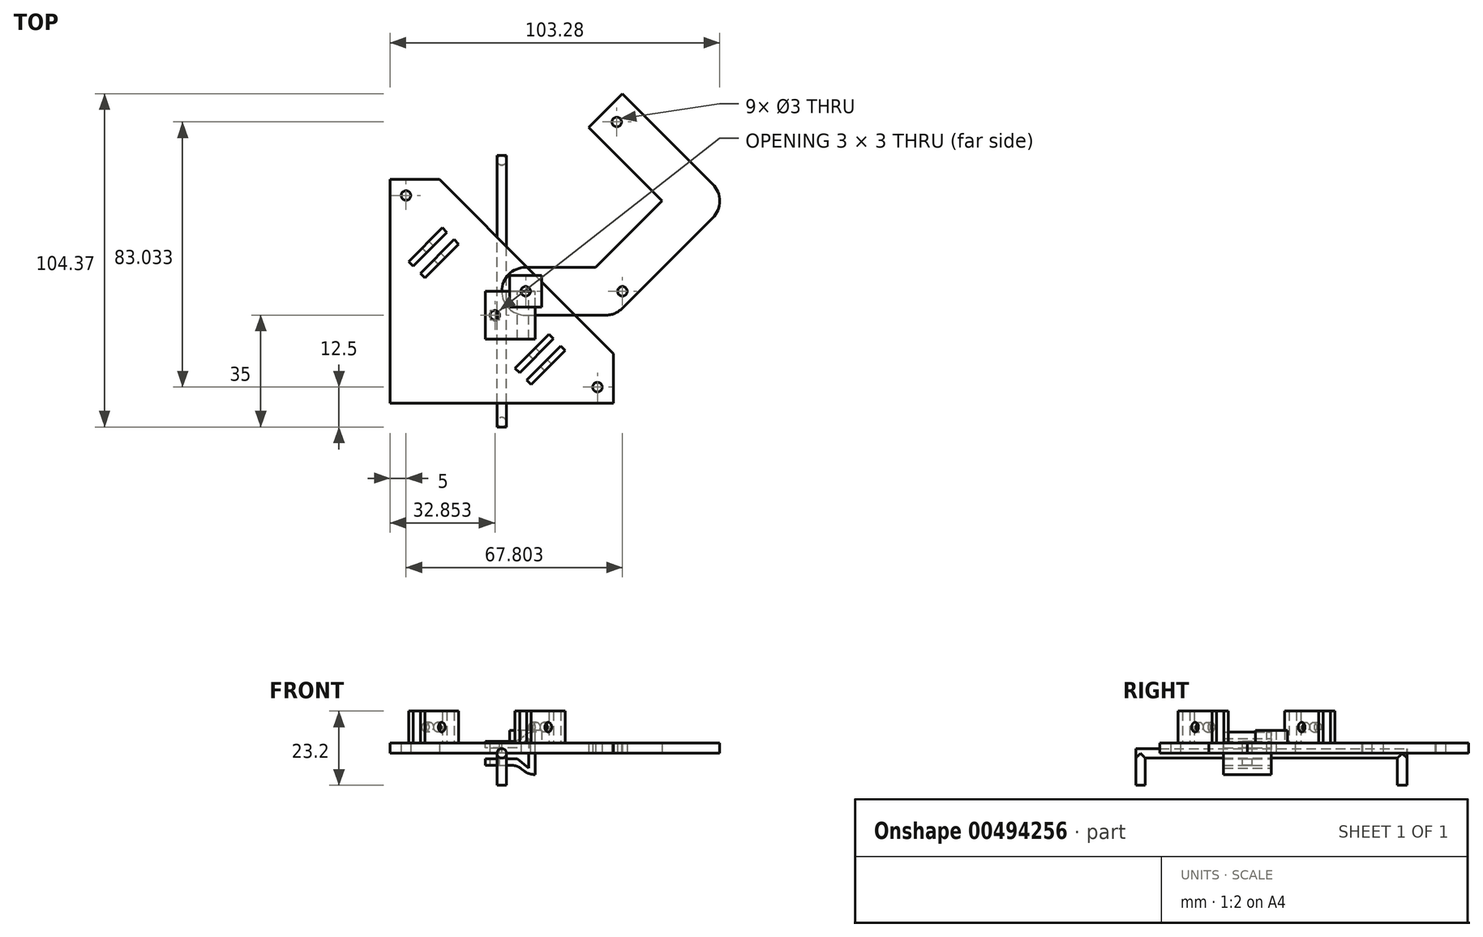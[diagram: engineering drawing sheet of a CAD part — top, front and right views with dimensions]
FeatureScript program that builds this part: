
annotation { "Feature Type Name" : "Feature", "Feature Type Description" : "" }
export const myFeature = defineFeature(function(context is Context, id is Id, definition is map)
    precondition{}
    {
        {
            var Q0;
            Q0=qCreatedBy(makeId("Top.planeOp"),FACE);
            var sketch = newSketch(context, id + "F0", { "sketchPlane" : qUnion([Q0])});
            skArc(sketch, "E0", {"start": v(7.5, 7.5) * mm, "mid": v(0, 0) * mm, "end": v(7.5, -7.5) * mm});
            skPoint(sketch, "E1", {"position": v(0, 0) * mm});
            skArc(sketch, "E2", {"start": v(32.5, -7.5) * mm, "mid": v(39.43, 2.87) * mm, "end": v(27.2, 5.3) * mm});
            skArc(sketch, "E3", {"start": v(55.48, 22.98) * mm, "mid": v(68.28, 28.28) * mm, "end": v(55.48, 33.59) * mm});
            skLineSegment(sketch, "E4", {"start": v(7.5, 7.5) * mm, "end": v(32.5, 7.5) * mm});
            skLineSegment(sketch, "E5", {"start": v(7.5, -7.5) * mm, "end": v(32.5, -7.5) * mm});
            skLineSegment(sketch, "E6", {"start": v(37.8, -5.3) * mm, "end": v(66.09, 22.98) * mm});
            skLineSegment(sketch, "E7", {"start": v(27.2, 5.3) * mm, "end": v(55.48, 33.59) * mm});
            skLineSegment(sketch, "E8", {"start": v(55.48, 22.98) * mm, "end": v(27.2, 51.27) * mm});
            skLineSegment(sketch, "E9", {"start": v(27.2, 51.27) * mm, "end": v(37.8, 61.87) * mm});
            skLineSegment(sketch, "E10", {"start": v(37.8, 61.87) * mm, "end": v(66.09, 33.59) * mm});
            skLineSegment(sketch, "E11", {"start": v(37.8, 61.87) * mm, "end": v(37.8, -5.3) * mm, "construction": true});
            skCircle(sketch, "E12", {"center": v(7.5, 0) * mm, "radius": 1.5 * mm});
            skCircle(sketch, "E13", {"center": v(37.8, 0) * mm, "radius": 1.5 * mm});
            skCircle(sketch, "E14", {"center": v(36.04, 53.03) * mm, "radius": 1.5 * mm});
            skSolve(sketch);
        }
        {
            var Q0;
            Q0 = qSketchRegion(id + "F0", true);
            extrude(context, id + "F1", {"entities" : qUnion([Q0]), "depth" : 3.2 * mm, "offsetDistance" : 25 * mm});
        }
        {
            var Q0;
            Q0=qCreatedBy(makeId("Top.planeOp"),FACE);
            var sketch = newSketch(context, id + "F2", { "sketchPlane" : qUnion([Q0])});
            skLineSegment(sketch, "E15.bottom", {"start": v(35, -35) * mm, "end": v(-35, -35) * mm});
            skLineSegment(sketch, "E15.top", {"start": v(-19.55, 35) * mm, "end": v(-35, 35) * mm});
            skLineSegment(sketch, "E15.left", {"start": v(35, -35) * mm, "end": v(35, -19.55) * mm});
            skLineSegment(sketch, "E15.right", {"start": v(-35, -35) * mm, "end": v(-35, 35) * mm});
            skPoint(sketch, "E15.middle", {"position": v(0, 0) * mm});
            skCircle(sketch, "E16", {"center": v(-30, 30) * mm, "radius": 1.5 * mm});
            skCircle(sketch, "E17", {"center": v(30, -30) * mm, "radius": 1.5 * mm});
            skLineSegment(sketch, "E18", {"start": v(-35, 35) * mm, "end": v(35, -35) * mm, "construction": true});
            skLineSegment(sketch, "E19", {"start": v(-19.55, 35) * mm, "end": v(35, -19.55) * mm});
            skSolve(sketch);
        }
        {
            var Q0;
            Q0=makeQuery(id+"F2.imprint","IMPRINT",FACE,{"disambiguationData":[TD([[makeQuery(id+"F2.imprint","IMPRINT",EDGE,{"derivedFrom":sQuery(id+"F2.wireOp",EDGE,"E15.bottom")}),-1.0]])]});
            extrude(context, id + "F3", {"entities" : qUnion([Q0]), "depth" : 3.2 * mm, "offsetDistance" : 25 * mm});
        }
        {
            var Q0;
            Q0=qCreatedBy(makeId("Front.planeOp"),FACE);
            var sketch = newSketch(context, id + "F4", { "sketchPlane" : qUnion([Q0])});
            skLineSegment(sketch, "E20", {"start": v(8.43, -4.62) * mm, "end": v(4.85, -1.75) * mm});
            skLineSegment(sketch, "E21", {"start": v(4.85, -1.75) * mm, "end": v(-5.15, -1.75) * mm});
            skLineSegment(sketch, "E22", {"start": v(-5.15, -1.75) * mm, "end": v(-5.15, -3.75) * mm});
            skLineSegment(sketch, "E23", {"start": v(-5.15, -3.75) * mm, "end": v(4.85, -3.75) * mm});
            skLineSegment(sketch, "E24", {"start": v(4.85, -3.75) * mm, "end": v(8.43, -6.62) * mm});
            skLineSegment(sketch, "E25", {"start": v(8.43, -6.62) * mm, "end": v(10.43, -6.62) * mm});
            skPoint(sketch, "E26", {"position": v(8.43, 0) * mm});
            skPoint(sketch, "E27", {"position": v(10.43, 0) * mm});
            skLineSegment(sketch, "E28", {"start": v(10.43, 0) * mm, "end": v(-7.22, 0) * mm, "construction": true});
            skLineSegment(sketch, "E29", {"start": v(8.43, -4.62) * mm, "end": v(8.43, 0) * mm});
            skLineSegment(sketch, "E30", {"start": v(10.43, -6.62) * mm, "end": v(10.43, 0) * mm});
            skLineSegment(sketch, "E31.MirrorCS", {"start": v(-5.15, 1.75) * mm, "end": v(-5.15, 3.75) * mm});
            skLineSegment(sketch, "E32.MirrorCS", {"start": v(8.43, 6.62) * mm, "end": v(10.43, 6.62) * mm});
            skLineSegment(sketch, "E33.MirrorCS", {"start": v(4.85, 1.75) * mm, "end": v(-5.15, 1.75) * mm});
            skLineSegment(sketch, "E34.MirrorCS", {"start": v(8.43, 4.62) * mm, "end": v(4.85, 1.75) * mm});
            skLineSegment(sketch, "E35.MirrorCS", {"start": v(4.85, 3.75) * mm, "end": v(8.43, 6.62) * mm});
            skLineSegment(sketch, "E36.MirrorCS", {"start": v(-5.15, 3.75) * mm, "end": v(4.85, 3.75) * mm});
            skLineSegment(sketch, "E37.MirrorCS", {"start": v(8.43, 4.62) * mm, "end": v(8.43, 0) * mm});
            skLineSegment(sketch, "E38.MirrorCS", {"start": v(10.43, 6.62) * mm, "end": v(10.43, 0) * mm});
            skSolve(sketch);
        }
        {
            var Q0;
            Q0 = qSketchRegion(id + "F4", true);
            extrude(context, id + "F5", {"entities" : qUnion([Q0]), "depth" : 15 * mm, "offsetDistance" : 25 * mm});
        }
        {
            var Q0;
            Q0=makeQuery(id+"F5.opExtrude","SWEPT_FACE",FACE,{"disambiguationData":[OSD([sQuery(id+"F4.wireOp",EDGE,"E36.MirrorCS")])]});
            var sketch = newSketch(context, id + "F6", { "sketchPlane" : qUnion([Q0])});
            skCircle(sketch, "E39", {"center": v(-2.15, -7.5) * mm, "radius": 1.5 * mm});
            skSolve(sketch);
        }
        {
            var Q0;
            Q0=makeQuery(id+"F6.imprint","IMPRINT",FACE,{"disambiguationData":[TD([[makeQuery(id+"F6.imprint","IMPRINT",EDGE,{"derivedFrom":sQuery(id+"F6.wireOp",EDGE,"E39")}),1.0]])]});
            extrude(context, id + "F7", {"entities" : qUnion([Q0]), "operationType" : NewBodyOperationType.REMOVE, "oppositeDirection" : true, "depth" : 25 * mm, "offsetDistance" : 25 * mm});
        }
        {
            var Q0;
            Q0=makeQuery(id+"F5.opExtrude","SWEPT_EDGE",EDGE,{"disambiguationData":[OSD([sQuery(id+"F4.wireOp",EDGE,"E35.MirrorCS"),sQuery(id+"F4.wireOp",EDGE,"E36.MirrorCS")])]});
            fillet(context, id + "F8", {"entities" : qUnion([Q0]), "radius" : 5 * mm, "tangentPropagation" : true, "allowEdgeOverflow" : false});
        }
        {
            var Q0;
            Q0=makeQuery(id+"F5.opExtrude","SWEPT_EDGE",EDGE,{"disambiguationData":[OSD([sQuery(id+"F4.wireOp",EDGE,"E23"),sQuery(id+"F4.wireOp",EDGE,"E24")])]});
            var Q1;
            Q1=makeQuery(id+"F5.opExtrude","SWEPT_EDGE",EDGE,{"disambiguationData":[OSD([sQuery(id+"F4.wireOp",EDGE,"E24"),sQuery(id+"F4.wireOp",EDGE,"E25")])]});
            var Q2;
            Q2=makeQuery(id+"F5.opExtrude","SWEPT_EDGE",EDGE,{"disambiguationData":[OSD([sQuery(id+"F4.wireOp",EDGE,"E32.MirrorCS"),sQuery(id+"F4.wireOp",EDGE,"E35.MirrorCS")])]});
            fillet(context, id + "F9", {"entities" : qUnion([Q0, Q1, Q2]), "radius" : 5 * mm, "tangentPropagation" : true, "allowEdgeOverflow" : false});
        }
        {
            var Q0;
            Q0=makeQuery(id+"F1.opExtrude","CAP_FACE",FACE,{"disambiguationData":[OSD([sQuery(id+"F0.wireOp",EDGE,"E0"),sQuery(id+"F0.wireOp",EDGE,"E2"),sQuery(id+"F0.wireOp",EDGE,"E3"),sQuery(id+"F0.wireOp",EDGE,"E4"),sQuery(id+"F0.wireOp",EDGE,"E5"),sQuery(id+"F0.wireOp",EDGE,"E6"),sQuery(id+"F0.wireOp",EDGE,"E7"),sQuery(id+"F0.wireOp",EDGE,"E8"),sQuery(id+"F0.wireOp",EDGE,"E9"),sQuery(id+"F0.wireOp",EDGE,"E10"),sQuery(id+"F0.wireOp",EDGE,"E12"),sQuery(id+"F0.wireOp",EDGE,"E13"),sQuery(id+"F0.wireOp",EDGE,"E14")])],"isStart":false});
            var sketch = newSketch(context, id + "F10", { "sketchPlane" : qUnion([Q0])});
            skLineSegment(sketch, "E40.bottom", {"start": v(12.5, -5) * mm, "end": v(2.5, -5) * mm});
            skLineSegment(sketch, "E40.top", {"start": v(12.5, 5) * mm, "end": v(2.5, 5) * mm});
            skLineSegment(sketch, "E40.left", {"start": v(12.5, -5) * mm, "end": v(12.5, 5) * mm});
            skLineSegment(sketch, "E40.right", {"start": v(2.5, -5) * mm, "end": v(2.5, 5) * mm});
            skPoint(sketch, "E40.middle", {"position": v(7.5, 0) * mm});
            skSolve(sketch);
        }
        {
            var Q0;
            Q0=makeQuery(id+"F10.imprint","IMPRINT",FACE,{"disambiguationData":[TD([[makeQuery(id+"F10.imprint","IMPRINT",EDGE,{"derivedFrom":sQuery(id+"F10.wireOp",EDGE,"E40.bottom")}),-1.0]])]});
            extrude(context, id + "F11", {"entities" : qUnion([Q0]), "depth" : 4 * mm, "offsetDistance" : 25 * mm});
        }
        {
            var Q0;
            Q0=makeQuery(id+"F3.opExtrude","CAP_FACE",FACE,{"disambiguationData":[OSD([sQuery(id+"F2.wireOp",EDGE,"E15.bottom"),sQuery(id+"F2.wireOp",EDGE,"E15.top"),sQuery(id+"F2.wireOp",EDGE,"E15.left"),sQuery(id+"F2.wireOp",EDGE,"E15.right"),sQuery(id+"F2.wireOp",EDGE,"E16"),sQuery(id+"F2.wireOp",EDGE,"E17"),sQuery(id+"F2.wireOp",EDGE,"E19")])],"isStart":true});
            var sketch = newSketch(context, id + "F12", { "sketchPlane" : qUnion([Q0])});
            skLineSegment(sketch, "E41", {"start": v(-25.5, -5.6) * mm, "end": v(-14.9, -16.2) * mm});
            skLineSegment(sketch, "E42", {"start": v(14.8, 13.49) * mm, "end": v(4.19, 24.1) * mm});
            skLineSegment(sketch, "E43", {"start": v(-25.5, -5.6) * mm, "end": v(-24.1, -4.19) * mm});
            skLineSegment(sketch, "E44", {"start": v(-14.9, -16.2) * mm, "end": v(-13.49, -14.8) * mm});
            skLineSegment(sketch, "E45", {"start": v(-13.49, -14.8) * mm, "end": v(-24.1, -4.19) * mm});
            skLineSegment(sketch, "E46", {"start": v(4.19, 24.1) * mm, "end": v(5.6, 25.5) * mm});
            skLineSegment(sketch, "E47", {"start": v(5.6, 25.5) * mm, "end": v(16.2, 14.9) * mm});
            skLineSegment(sketch, "E48", {"start": v(16.2, 14.9) * mm, "end": v(14.8, 13.49) * mm});
            skLineSegment(sketch, "E49", {"start": v(-8.96, -24.41) * mm, "end": v(-29.1, -4.27) * mm, "construction": true});
            skLineSegment(sketch, "E50.MirrorCS", {"start": v(-27.77, -7.87) * mm, "end": v(-29.19, -9.28) * mm});
            skLineSegment(sketch, "E51.MirrorCS", {"start": v(-18.58, -19.89) * mm, "end": v(-29.19, -9.28) * mm});
            skLineSegment(sketch, "E52.MirrorCS", {"start": v(-27.77, -7.87) * mm, "end": v(-17.17, -18.47) * mm});
            skLineSegment(sketch, "E53.MirrorCS", {"start": v(-17.17, -18.47) * mm, "end": v(-18.58, -19.89) * mm});
            skLineSegment(sketch, "E54", {"start": v(24.41, 8.96) * mm, "end": v(5.32, 28.06) * mm, "construction": true});
            skLineSegment(sketch, "E55.MirrorCS", {"start": v(7.87, 27.77) * mm, "end": v(18.47, 17.17) * mm});
            skLineSegment(sketch, "E56.MirrorCS", {"start": v(19.89, 18.58) * mm, "end": v(9.28, 29.19) * mm});
            skLineSegment(sketch, "E57.MirrorCS", {"start": v(18.47, 17.17) * mm, "end": v(19.89, 18.58) * mm});
            skLineSegment(sketch, "E58.MirrorCS", {"start": v(9.28, 29.19) * mm, "end": v(7.87, 27.77) * mm});
            skSolve(sketch);
        }
        {
            var Q0;
            Q0=makeQuery(id+"F12.imprint","IMPRINT",FACE,{"disambiguationData":[TD([[makeQuery(id+"F12.imprint","IMPRINT",EDGE,{"derivedFrom":sQuery(id+"F12.wireOp",EDGE,"E50.MirrorCS")}),1.0]])]});
            var Q1;
            Q1=makeQuery(id+"F12.imprint","IMPRINT",FACE,{"disambiguationData":[TD([[makeQuery(id+"F12.imprint","IMPRINT",EDGE,{"derivedFrom":sQuery(id+"F12.wireOp",EDGE,"E41")}),1.0]])]});
            var Q2;
            Q2=makeQuery(id+"F12.imprint","IMPRINT",FACE,{"disambiguationData":[TD([[makeQuery(id+"F12.imprint","IMPRINT",EDGE,{"derivedFrom":sQuery(id+"F12.wireOp",EDGE,"E42")}),-1.0]])]});
            var Q3;
            Q3=makeQuery(id+"F12.imprint","IMPRINT",FACE,{"disambiguationData":[TD([[makeQuery(id+"F12.imprint","IMPRINT",EDGE,{"derivedFrom":sQuery(id+"F12.wireOp",EDGE,"E55.MirrorCS")}),1.0]])]});
            extrude(context, id + "F13", {"entities" : qUnion([Q0, Q1, Q2, Q3]), "operationType" : NewBodyOperationType.ADD, "oppositeDirection" : true, "depth" : 13.2 * mm, "offsetDistance" : 25 * mm});
        }
        {
            var Q0;
            Q0=makeQuery(id+"F13.opExtrude","SWEPT_FACE",FACE,{"disambiguationData":[OSD([sQuery(id+"F12.wireOp",EDGE,"E51.MirrorCS")])]});
            var sketch = newSketch(context, id + "F14", { "sketchPlane" : qUnion([Q0])});
            skCircle(sketch, "E59", {"center": v(6.58, 8.2) * mm, "radius": 1.5 * mm});
            skPoint(sketch, "E59.centerSnap0", {"position": v(6.58, 13.2) * mm});
            skSolve(sketch);
        }
        {
            var Q0;
            Q0=makeQuery(id+"F14.imprint","IMPRINT",FACE,{"disambiguationData":[TD([[makeQuery(id+"F14.imprint","IMPRINT",EDGE,{"derivedFrom":sQuery(id+"F14.wireOp",EDGE,"E59")}),1.0]])]});
            var Q1;
            Q1=sQuery(id+"F14.wireOp",EDGE,"E59");
            extrude(context, id + "F15", {"entities" : qUnion([Q0]), "operationType" : NewBodyOperationType.REMOVE, "surfaceEntities" : qUnion([Q1]), "oppositeDirection" : true, "depth" : 60 * mm, "offsetDistance" : 25 * mm});
        }
        {
            var Q0;
            Q0=qCreatedBy(makeId("Front.planeOp"),FACE);
            var sketch = newSketch(context, id + "F16", { "sketchPlane" : qUnion([Q0])});
            skCircle(sketch, "E60", {"center": v(0, 0) * mm, "radius": 1.5 * mm});
            skSolve(sketch);
        }
        {
            var Q0;
            Q0=makeQuery(id+"F16.imprint","IMPRINT",FACE,{"disambiguationData":[TD([[makeQuery(id+"F16.imprint","IMPRINT",EDGE,{"derivedFrom":sQuery(id+"F16.wireOp",EDGE,"E60")}),1.0]])]});
            var Q1;
            Q1=sQuery(id+"F16.wireOp",EDGE,"E60");
            extrude(context, id + "F17", {"entities" : qUnion([Q0]), "surfaceEntities" : qUnion([Q1]), "depth" : 85 * mm, "offsetDistance" : 25 * mm, "symmetric" : true});
        }
        {
            var Q0;
            Q0=qCreatedBy(makeId("Top.planeOp"),FACE);
            var sketch = newSketch(context, id + "F18", { "sketchPlane" : qUnion([Q0])});
            skCircle(sketch, "E61", {"center": v(0, -41) * mm, "radius": 1.5 * mm});
            skSolve(sketch);
        }
        {
            var Q0;
            Q0 = qSketchRegion(id + "F18", true);
            var Q1;
            Q1=sQuery(id+"F18.wireOp",EDGE,"E61");
            extrude(context, id + "F19", {"entities" : qUnion([Q0]), "operationType" : NewBodyOperationType.ADD, "surfaceEntities" : qUnion([Q1]), "oppositeDirection" : true, "depth" : 10 * mm, "offsetDistance" : 25 * mm});
        }
        {
            var Q0;
            Q0=qCreatedBy(makeId("Top.planeOp"),FACE);
            var sketch = newSketch(context, id + "F20", { "sketchPlane" : qUnion([Q0])});
            skCircle(sketch, "E62", {"center": v(0, 41) * mm, "radius": 1.5 * mm});
            skSolve(sketch);
        }
        {
            var Q0;
            Q0 = qSketchRegion(id + "F20", true);
            extrude(context, id + "F21", {"entities" : qUnion([Q0]), "operationType" : NewBodyOperationType.ADD, "oppositeDirection" : true, "depth" : 10 * mm, "offsetDistance" : 25 * mm});
        }
    });
